# Revit family: QF_ELECTROLUXPROFESSIONAL_1L0A44_WE170P_E
name_source: partatom
category: Attrezzature speciali
units: mm (PartAtom-declared; Revit-internal decimal feet)

## family parameters
Basato su piano di lavoro = No
Condiviso = No
Punto di calcolo locali = No
Quota connettore circolare = Usa diametro
Sempre verticale = Sì
Taglio con vuoti quando caricato = No
Tipo di parte = Normale

## types (6) — shared parameters
Depth = 620 mm
Depth Actual = 624 mm
Height = 847 mm
Height Actual = 850 mm
Latent Heat Output = 0.0
Length Actual = 597 mm
Modello = WE170P
Phase = 1
Produttore = Electrolux Professional
Sensible Heat Output = 0.0
URL = www.electroluxprofessional.com
Watts = 2200 W
Weight = 80.5
Width = 597 mm
zero-valued in all types: Gas KW, Prospetto di default, Steam Pounds per Hour

## per-type parameters (varying)
| type | Cycle | Descrizione | Item Number | Volts |
| 914535305 | 60 Hz | myPRO SMART PROFESSIONAL WASHER WE170P 8KG PUMP 230-240/60/1N 2,2KW SYMBOLS SCHUKO SST/DARK BLUE | 1L0BJH | 230 V |
| 914535307 | 50 Hz | myPRO SMART PROFESSIONAL WASHER WE170P 8KG PUMP 230-240/50/1N 2,2KW EN PLUG-AU SST/DARK BLUE | 1L0BJK | 240 V |
| 914535315 | 50 Hz | myPRO SMART PROFESSIONAL WASHER WE170P 8KG PUMP 230-240/50/1N 2,2KW EN PLUG-UK SST/DARK BLUE | 1LSP93 | 230 V |
| 914535316 | 50 Hz | myPRO SMART PROFESSIONAL WASHER WE170P 8KG PUMP 230-240/50/1N 2,2KW DE SCHUKO SST/DARK BLUE | 1LSP94 | 230 V |
| 914535317 | 50 Hz | myPRO SMART PROFESSIONAL WASHER WE170P 8KG PUMP 230-240/50/1N 2,2KW FR SCHUKO SST/DARK BLUE | 1LSP95 | 230 V |
| 914535318 | 50 Hz | myPRO SMART PROFESSIONAL WASHER WE170P 8KG PUMP 230-240/50/1N 2,2KW SYMBOLS SCHUKO SST/DARK BLUE | 1LSP96 | 230 V |

## geometry (parser evidence)
native form markers: Sweep x2
no freeform markers — native parametric forms only
